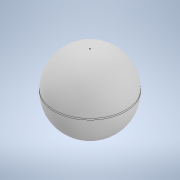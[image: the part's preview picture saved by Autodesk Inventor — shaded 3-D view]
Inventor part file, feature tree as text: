
AUTODESK INVENTOR PART (.ipt)
format: ipt  version: 2021 (Build 250183000, 183)  size: 144,384 bytes
history: native  units: in
note: dims shown in document units (in); Inventor stores cm internally (conversion verified against a paired STEP export)
features: extrude x1, fillet x1, sketch x1
ambient origin geometry x8: Origin, YZ Plane, XZ Plane, XY Plane, X Axis, Y Axis, Z Axis, Center Point
bodies: Solid1 (feature_tree)
feature tree (3):
  extrude  "Extrusion1"  Depth=0.1969in TaperAngle=0.0deg
  fillet  "Fillet1"  Radius=0.0965in
  sketch  "Sketch1"  dims[d0=0.1969in d1=0.1969in d2=0.0in d3=0.0965in]
